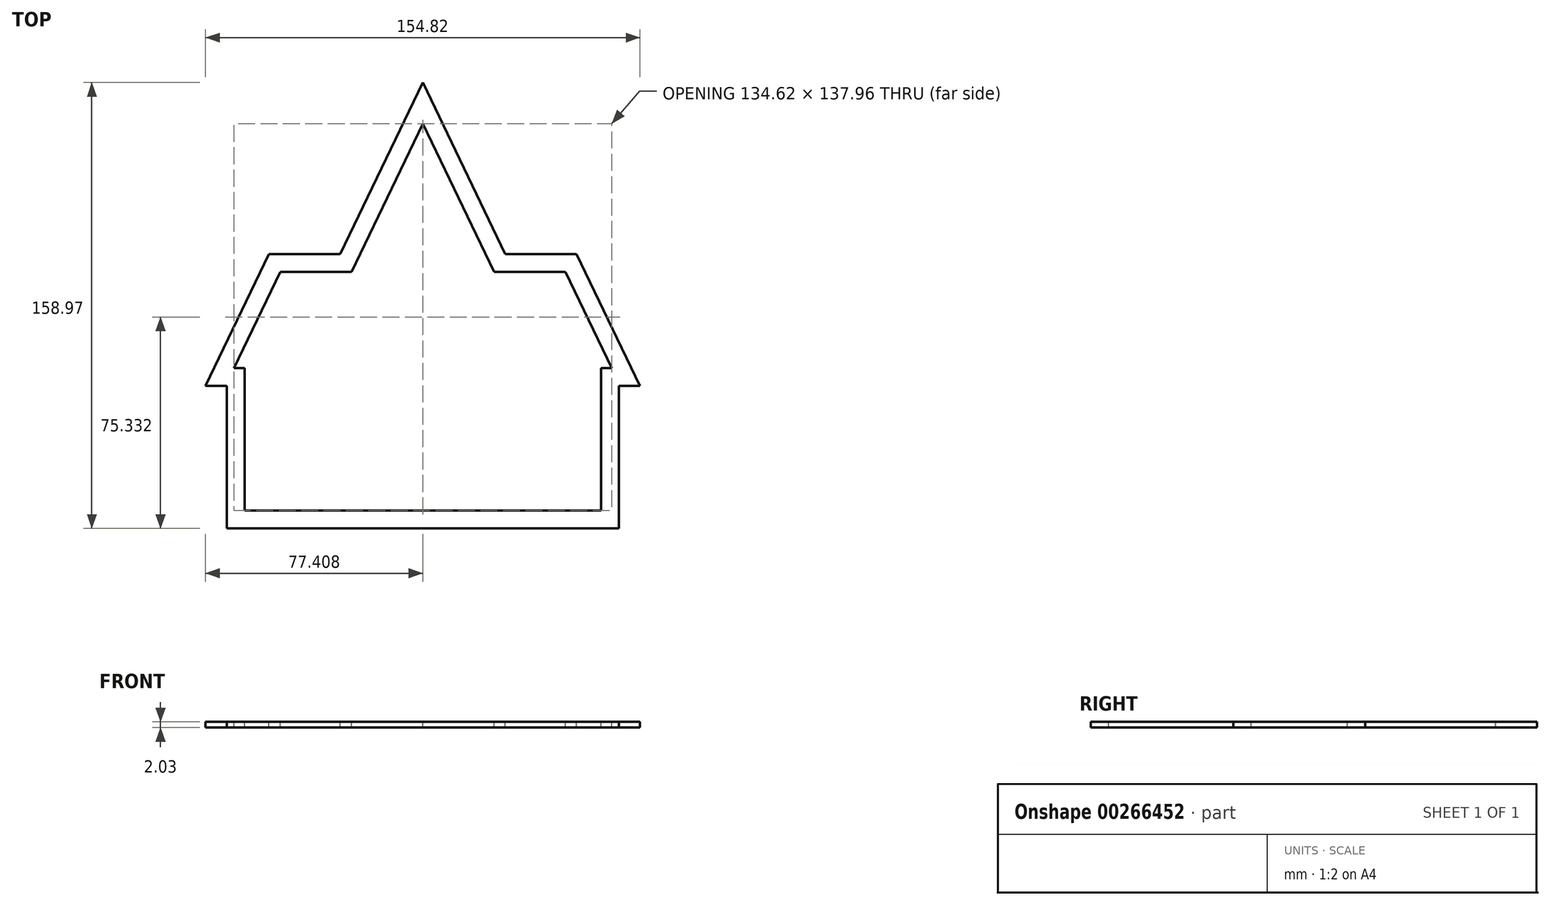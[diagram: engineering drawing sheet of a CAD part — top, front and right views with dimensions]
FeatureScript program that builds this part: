
annotation { "Feature Type Name" : "Feature", "Feature Type Description" : "" }
export const myFeature = defineFeature(function(context is Context, id is Id, definition is map)
    precondition{}
    {
        {
            var Q0;
            Q0=qCreatedBy(makeId("Top.planeOp"),FACE);
            var sketch = newSketch(context, id + "F0", { "sketchPlane" : qUnion([Q0])});
            skLineSegment(sketch, "E0", {"start": v(-58.74, -50.8) * mm, "end": v(68.26, -50.8) * mm});
            skLineSegment(sketch, "E1", {"start": v(-58.74, -50.8) * mm, "end": v(-58.74, 0) * mm});
            skLineSegment(sketch, "E2", {"start": v(68.26, -50.8) * mm, "end": v(68.26, 0) * mm});
            skLineSegment(sketch, "E3", {"start": v(-61.82, 1.52) * mm, "end": v(-46.04, 34.34) * mm});
            skLineSegment(sketch, "E4", {"start": v(-46.04, 34.34) * mm, "end": v(-22.33, 34.34) * mm});
            skLineSegment(sketch, "E5", {"start": v(71.34, 1.52) * mm, "end": v(55.56, 34.34) * mm});
            skLineSegment(sketch, "E6", {"start": v(55.56, 34.34) * mm, "end": v(30.16, 34.34) * mm});
            skLineSegment(sketch, "E7", {"start": v(-20.64, 34.34) * mm, "end": v(-36.05, 2.29) * mm});
            skLineSegment(sketch, "E8", {"start": v(30.16, 34.34) * mm, "end": v(45.57, 2.29) * mm});
            skLineSegment(sketch, "E9", {"start": v(68.26, 0) * mm, "end": v(42.86, 0) * mm});
            skLineSegment(sketch, "E10", {"start": v(42.86, 0) * mm, "end": v(45.57, 2.29) * mm});
            skLineSegment(sketch, "E11", {"start": v(-58.74, 0) * mm, "end": v(-33.34, 0) * mm});
            skLineSegment(sketch, "E12", {"start": v(-33.34, 0) * mm, "end": v(-36.05, 2.29) * mm});
            skLineSegment(sketch, "E13", {"start": v(30.16, 34.34) * mm, "end": v(4.76, 87.16) * mm});
            skLineSegment(sketch, "E14", {"start": v(4.76, 87.16) * mm, "end": v(-20.64, 34.34) * mm});
            skLineSegment(sketch, "E15", {"start": v(4.76, 59.42) * mm, "end": v(0.83, 51.25) * mm});
            skLineSegment(sketch, "E16", {"start": v(4.76, 59.42) * mm, "end": v(8.7, 51.24) * mm});
            skLineSegment(sketch, "E17", {"start": v(14.66, 37.8) * mm, "end": v(14.66, 26.12) * mm});
            skLineSegment(sketch, "E18", {"start": v(-5.15, 37.8) * mm, "end": v(-5.15, 26.12) * mm});
            skLineSegment(sketch, "E19", {"start": v(-5.15, 13.42) * mm, "end": v(-0.2, 13.42) * mm});
            skLineSegment(sketch, "E20", {"start": v(9.71, 13.42) * mm, "end": v(9.71, 25.1) * mm});
            skLineSegment(sketch, "E21", {"start": v(-0.2, 49.12) * mm, "end": v(-0.2, 38.82) * mm});
            skLineSegment(sketch, "E22", {"start": v(14.66, 26.12) * mm, "end": v(9.71, 26.12) * mm});
            skLineSegment(sketch, "E23", {"start": v(14.66, 38.82) * mm, "end": v(9.71, 38.82) * mm});
            skLineSegment(sketch, "E24.0", {"start": v(-58.74, 1.52) * mm, "end": v(-38.11, 1.52) * mm});
            skLineSegment(sketch, "E24.1", {"start": v(-22.33, 34.34) * mm, "end": v(-38.11, 1.52) * mm});
            skLineSegment(sketch, "E25", {"start": v(-58.74, 1.52) * mm, "end": v(-61.82, 1.52) * mm});
            skLineSegment(sketch, "E26.0", {"start": v(68.26, 1.52) * mm, "end": v(47.63, 1.52) * mm});
            skLineSegment(sketch, "E26.1", {"start": v(31.85, 34.34) * mm, "end": v(47.63, 1.52) * mm});
            skLineSegment(sketch, "E27", {"start": v(68.26, 1.52) * mm, "end": v(71.34, 1.52) * mm});
            skLineSegment(sketch, "E28", {"start": v(-22.33, 34.34) * mm, "end": v(-20.64, 34.34) * mm});
            skLineSegment(sketch, "E29", {"start": v(-61.82, 1.52) * mm, "end": v(-62.55, 0) * mm});
            skLineSegment(sketch, "E30", {"start": v(-62.55, 0) * mm, "end": v(-58.74, 0) * mm});
            skLineSegment(sketch, "E31", {"start": v(71.34, 1.52) * mm, "end": v(72.07, 0) * mm});
            skLineSegment(sketch, "E32", {"start": v(68.26, 0) * mm, "end": v(72.07, 0) * mm});
            skLineSegment(sketch, "E33.0", {"start": v(31.44, 36.37) * mm, "end": v(4.76, 91.85) * mm});
            skLineSegment(sketch, "E33.1", {"start": v(56.84, 36.37) * mm, "end": v(31.44, 36.37) * mm});
            skLineSegment(sketch, "E33.2", {"start": v(72.68, 3.42) * mm, "end": v(56.84, 36.37) * mm});
            skLineSegment(sketch, "E33.3", {"start": v(-63.16, 3.42) * mm, "end": v(-65.78, -2.03) * mm});
            skLineSegment(sketch, "E33.4", {"start": v(-63.16, 3.42) * mm, "end": v(-47.32, 36.37) * mm});
            skLineSegment(sketch, "E33.5", {"start": v(-47.32, 36.37) * mm, "end": v(-23.46, 36.37) * mm});
            skLineSegment(sketch, "E33.6", {"start": v(-23.46, 36.37) * mm, "end": v(-21.92, 36.37) * mm});
            skLineSegment(sketch, "E33.7", {"start": v(-65.78, -2.03) * mm, "end": v(-60.77, -2.03) * mm});
            skLineSegment(sketch, "E33.8", {"start": v(-60.77, -52.83) * mm, "end": v(-60.77, -2.03) * mm});
            skLineSegment(sketch, "E33.9", {"start": v(-60.77, -52.83) * mm, "end": v(70.3, -52.83) * mm});
            skLineSegment(sketch, "E33.10", {"start": v(4.76, 91.85) * mm, "end": v(-21.92, 36.37) * mm});
            skLineSegment(sketch, "E33.11", {"start": v(70.3, -52.83) * mm, "end": v(70.3, -2.03) * mm});
            skLineSegment(sketch, "E33.12", {"start": v(70.3, -2.03) * mm, "end": v(75.3, -2.03) * mm});
            skLineSegment(sketch, "E33.13", {"start": v(72.68, 3.42) * mm, "end": v(75.3, -2.03) * mm});
            skLineSegment(sketch, "E34.0", {"start": v(-6.16, 39.05) * mm, "end": v(-6.16, 12.4) * mm});
            skLineSegment(sketch, "E34.1", {"start": v(4.76, 61.76) * mm, "end": v(-6.16, 39.05) * mm});
            skLineSegment(sketch, "E34.2", {"start": v(-6.16, 12.4) * mm, "end": v(15.68, 12.4) * mm});
            skLineSegment(sketch, "E34.3", {"start": v(15.68, 39.05) * mm, "end": v(15.68, 12.4) * mm});
            skLineSegment(sketch, "E34.4", {"start": v(4.76, 61.76) * mm, "end": v(15.68, 39.05) * mm});
            skLineSegment(sketch, "E35", {"start": v(14.66, 37.8) * mm, "end": v(9.71, 37.8) * mm});
            skLineSegment(sketch, "E36", {"start": v(-5.15, 25.1) * mm, "end": v(-0.2, 25.1) * mm});
            skLineSegment(sketch, "E37", {"start": v(0.83, 13.42) * mm, "end": v(0.83, 25.1) * mm});
            skLineSegment(sketch, "E38", {"start": v(9.71, 13.42) * mm, "end": v(8.7, 13.42) * mm});
            skLineSegment(sketch, "E39", {"start": v(8.7, 13.42) * mm, "end": v(8.7, 25.1) * mm});
            skLineSegment(sketch, "E40.trimOffspring", {"start": v(-0.2, 49.12) * mm, "end": v(-5.15, 38.82) * mm});
            skLineSegment(sketch, "E41.trimOffspring", {"start": v(9.71, 49.12) * mm, "end": v(14.66, 38.82) * mm});
            skLineSegment(sketch, "E42.trimOffspring", {"start": v(-0.2, 37.8) * mm, "end": v(-0.2, 26.12) * mm});
            skLineSegment(sketch, "E43.trimOffspring", {"start": v(-0.2, 38.82) * mm, "end": v(-5.15, 38.82) * mm});
            skLineSegment(sketch, "E44.trimOffspring", {"start": v(0.83, 38.82) * mm, "end": v(0.83, 51.25) * mm});
            skLineSegment(sketch, "E45.trimOffspring", {"start": v(-0.2, 37.8) * mm, "end": v(-5.15, 37.8) * mm});
            skLineSegment(sketch, "E46.trimOffspring", {"start": v(8.7, 38.82) * mm, "end": v(8.7, 51.24) * mm});
            skLineSegment(sketch, "E47.trimOffspring", {"start": v(8.7, 38.82) * mm, "end": v(0.83, 38.82) * mm});
            skLineSegment(sketch, "E48.trimOffspring", {"start": v(9.71, 38.82) * mm, "end": v(9.71, 49.12) * mm});
            skLineSegment(sketch, "E49.trimOffspring", {"start": v(8.7, 37.8) * mm, "end": v(0.83, 37.8) * mm});
            skLineSegment(sketch, "E50.trimOffspring", {"start": v(14.66, 25.1) * mm, "end": v(14.66, 13.42) * mm});
            skLineSegment(sketch, "E51.trimOffspring", {"start": v(9.71, 26.12) * mm, "end": v(9.71, 37.8) * mm});
            skLineSegment(sketch, "E52.trimOffspring", {"start": v(8.7, 26.12) * mm, "end": v(8.7, 37.8) * mm});
            skLineSegment(sketch, "E53.trimOffspring", {"start": v(0.83, 26.12) * mm, "end": v(0.83, 37.8) * mm});
            skLineSegment(sketch, "E54.trimOffspring", {"start": v(-0.2, 25.1) * mm, "end": v(-0.2, 13.42) * mm});
            skLineSegment(sketch, "E55.trimOffspring", {"start": v(-5.15, 25.1) * mm, "end": v(-5.15, 13.42) * mm});
            skLineSegment(sketch, "E56.trimOffspring", {"start": v(-0.2, 26.12) * mm, "end": v(-5.15, 26.12) * mm});
            skLineSegment(sketch, "E57.trimOffspring", {"start": v(0.83, 25.1) * mm, "end": v(8.7, 25.1) * mm});
            skLineSegment(sketch, "E58.trimOffspring", {"start": v(8.7, 26.12) * mm, "end": v(0.83, 26.12) * mm});
            skLineSegment(sketch, "E59.trimOffspring", {"start": v(9.71, 25.1) * mm, "end": v(14.66, 25.1) * mm});
            skLineSegment(sketch, "E60.trimOffspring", {"start": v(9.71, 13.42) * mm, "end": v(14.66, 13.42) * mm});
            skLineSegment(sketch, "E61.trimOffspring", {"start": v(0.83, 13.42) * mm, "end": v(8.7, 13.42) * mm});
            skLineSegment(sketch, "E62", {"start": v(-5.32, 66.2) * mm, "end": v(14.84, 66.2) * mm});
            skLineSegment(sketch, "E63", {"start": v(-8.58, 59.42) * mm, "end": v(18.1, 59.42) * mm});
            skLineSegment(sketch, "E64", {"start": v(-18.38, 39.05) * mm, "end": v(-6.16, 39.05) * mm});
            skLineSegment(sketch, "E65", {"start": v(-20.64, 34.34) * mm, "end": v(-6.16, 34.34) * mm});
            skLineSegment(sketch, "E66", {"start": v(15.68, 39.05) * mm, "end": v(27.9, 39.05) * mm});
            skLineSegment(sketch, "E67", {"start": v(30.16, 34.34) * mm, "end": v(15.68, 34.34) * mm});
            skLineSegment(sketch, "E68", {"start": v(40.22, 13.42) * mm, "end": v(-30.7, 13.42) * mm});
            skLineSegment(sketch, "E69", {"start": v(-32.53, 9.6) * mm, "end": v(42.05, 9.6) * mm});
            skLineSegment(sketch, "E70.0", {"start": v(34.15, 40.69) * mm, "end": v(4.76, 101.82) * mm});
            skLineSegment(sketch, "E70.1", {"start": v(59.55, 40.69) * mm, "end": v(34.15, 40.69) * mm});
            skLineSegment(sketch, "E70.2", {"start": v(-72.65, -6.35) * mm, "end": v(-65.1, -6.35) * mm});
            skLineSegment(sketch, "E70.3", {"start": v(-67.05, 5.3) * mm, "end": v(-72.65, -6.35) * mm});
            skLineSegment(sketch, "E70.4", {"start": v(-67.05, 5.3) * mm, "end": v(-50.03, 40.69) * mm});
            skLineSegment(sketch, "E70.5", {"start": v(-50.03, 40.69) * mm, "end": v(-24.63, 40.69) * mm});
            skLineSegment(sketch, "E70.6", {"start": v(-65.1, -57.15) * mm, "end": v(-65.1, -6.35) * mm});
            skLineSegment(sketch, "E70.7", {"start": v(-65.1, -57.15) * mm, "end": v(74.6, -57.15) * mm});
            skLineSegment(sketch, "E70.8", {"start": v(4.76, 101.82) * mm, "end": v(-24.63, 40.69) * mm});
            skLineSegment(sketch, "E70.9", {"start": v(74.6, -57.15) * mm, "end": v(74.6, -6.35) * mm});
            skLineSegment(sketch, "E70.10", {"start": v(74.6, -6.35) * mm, "end": v(82.17, -6.35) * mm});
            skLineSegment(sketch, "E70.11", {"start": v(76.57, 5.3) * mm, "end": v(82.17, -6.35) * mm});
            skLineSegment(sketch, "E70.12", {"start": v(76.57, 5.3) * mm, "end": v(59.55, 40.69) * mm});
            skSolve(sketch);
        }
        {
            var Q0;
            Q0=makeQuery(id+"F0.imprint","IMPRINT",FACE,{"disambiguationData":[TD([[makeQuery(id+"F0.imprint","IMPRINT",EDGE,{"derivedFrom":sQuery(id+"F0.wireOp",EDGE,"E0")}),-1.0]])]});
            var Q1;
            Q1=makeQuery(id+"F0.imprint","IMPRINT",FACE,{"disambiguationData":[TD([[makeQuery(id+"F0.imprint","IMPRINT",EDGE,{"derivedFrom":sQuery(id+"F0.wireOp",EDGE,"E33.0")}),-1.0]])]});
            extrude(context, id + "F1", {"entities" : qUnion([Q0, Q1]), "oppositeDirection" : true, "depth" : 2.03 * mm});
        }
    });
